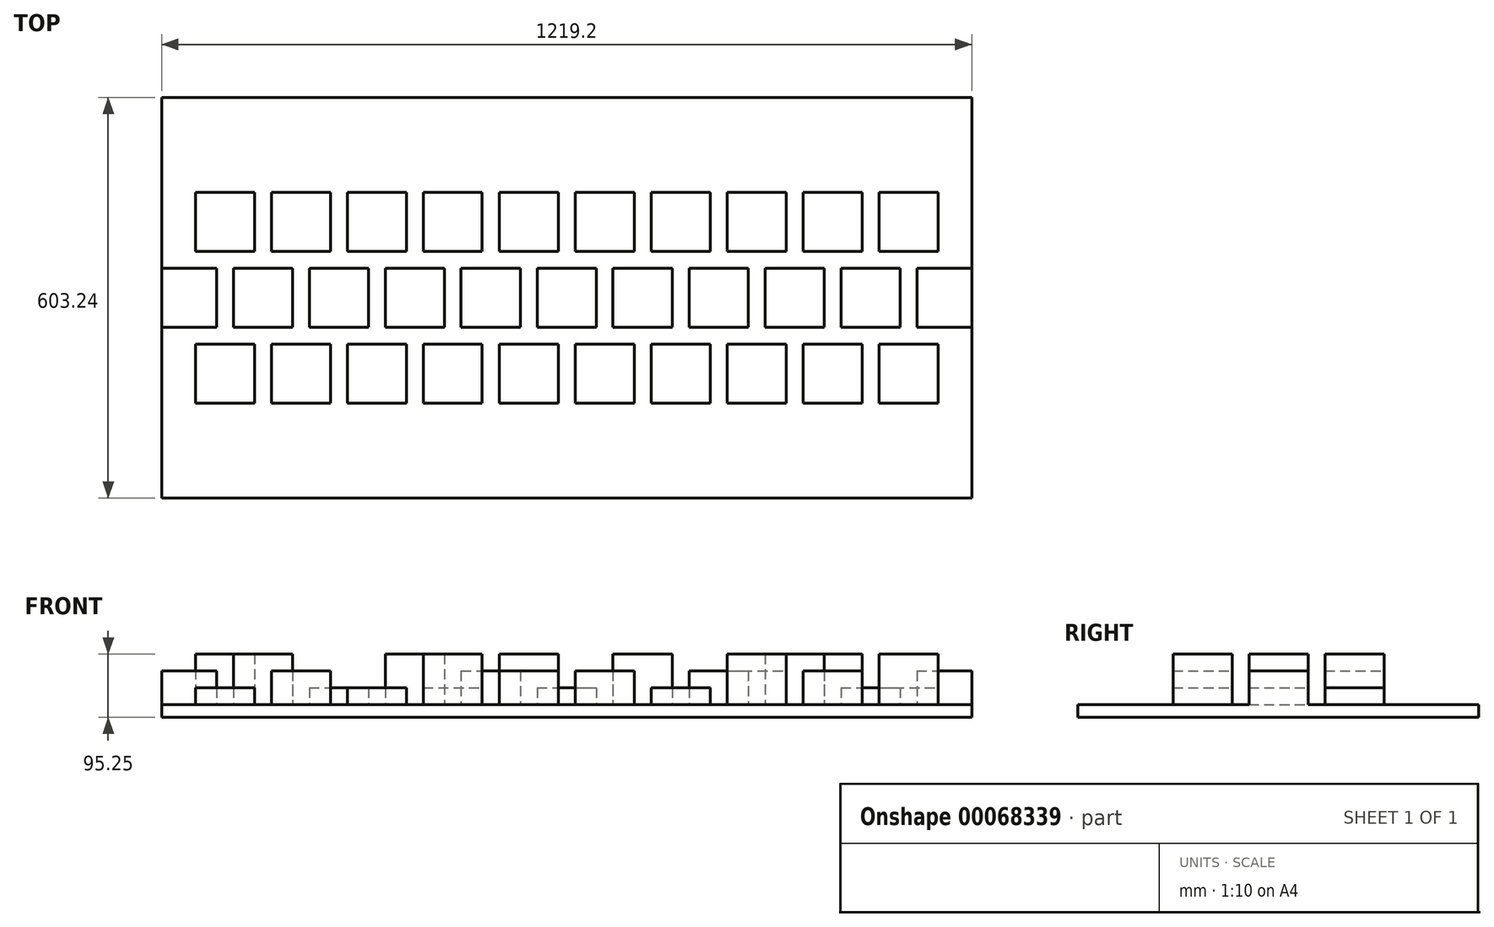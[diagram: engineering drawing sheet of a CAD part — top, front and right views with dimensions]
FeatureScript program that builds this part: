
annotation { "Feature Type Name" : "Feature", "Feature Type Description" : "" }
export const myFeature = defineFeature(function(context is Context, id is Id, definition is map)
    precondition{}
    {
        {
            var Q0;
            Q0=qCreatedBy(makeId("Top.planeOp"),FACE);
            var sketch = newSketch(context, id + "F0", { "sketchPlane" : qUnion([Q0])});
            skLineSegment(sketch, "E0.rect.bottom", {"start": v(-609.6, 301.63) * mm, "end": v(609.6, 301.63) * mm});
            skLineSegment(sketch, "E0.rect.top", {"start": v(-609.6, -301.63) * mm, "end": v(609.6, -301.63) * mm});
            skLineSegment(sketch, "E0.rect.left", {"start": v(-609.6, 301.63) * mm, "end": v(-609.6, -301.62) * mm});
            skLineSegment(sketch, "E0.rect.right", {"start": v(609.6, 301.63) * mm, "end": v(609.6, -301.62) * mm});
            skPoint(sketch, "E0.rect.middle", {"position": v(0, 0) * mm});
            skLineSegment(sketch, "E1", {"start": v(-709.91, -158.62) * mm, "end": v(803.28, -158.62) * mm, "construction": true});
            skLineSegment(sketch, "E2", {"start": v(803.28, 69.98) * mm, "end": v(-709.91, 69.98) * mm, "construction": true});
            skLineSegment(sketch, "E3", {"start": v(-709.91, -44.32) * mm, "end": v(803.28, -44.32) * mm, "construction": true});
            skLineSegment(sketch, "E4.bottom", {"start": v(-558.8, -158.62) * mm, "end": v(-469.9, -158.62) * mm});
            skLineSegment(sketch, "E4.top", {"start": v(-558.8, -69.72) * mm, "end": v(-469.9, -69.72) * mm});
            skLineSegment(sketch, "E4.left", {"start": v(-558.8, -158.62) * mm, "end": v(-558.8, -69.72) * mm});
            skLineSegment(sketch, "E4.right", {"start": v(-469.9, -158.62) * mm, "end": v(-469.9, -69.72) * mm});
            skLineSegment(sketch, "E5", {"start": v(469.9, -301.62) * mm, "end": v(469.9, 301.63) * mm, "construction": true});
            skLineSegment(sketch, "E6.0.1.0", {"start": v(-558.8, 69.98) * mm, "end": v(-469.9, 69.98) * mm});
            skLineSegment(sketch, "E6.0.1.1", {"start": v(-558.8, 158.88) * mm, "end": v(-469.9, 158.88) * mm});
            skLineSegment(sketch, "E6.0.1.2", {"start": v(-469.9, 69.98) * mm, "end": v(-469.9, 158.88) * mm});
            skLineSegment(sketch, "E6.0.1.3", {"start": v(-558.8, 69.98) * mm, "end": v(-558.8, 158.88) * mm});
            skLineSegment(sketch, "E6.1.0.0", {"start": v(-444.5, -158.62) * mm, "end": v(-355.6, -158.62) * mm});
            skLineSegment(sketch, "E6.1.0.1", {"start": v(-444.5, -69.72) * mm, "end": v(-355.6, -69.72) * mm});
            skLineSegment(sketch, "E6.1.0.2", {"start": v(-355.6, -158.62) * mm, "end": v(-355.6, -69.72) * mm});
            skLineSegment(sketch, "E6.1.0.3", {"start": v(-444.5, -158.62) * mm, "end": v(-444.5, -69.72) * mm});
            skLineSegment(sketch, "E6.1.1.0", {"start": v(-444.5, 69.98) * mm, "end": v(-355.6, 69.98) * mm});
            skLineSegment(sketch, "E6.1.1.1", {"start": v(-444.5, 158.88) * mm, "end": v(-355.6, 158.88) * mm});
            skLineSegment(sketch, "E6.1.1.2", {"start": v(-355.6, 69.98) * mm, "end": v(-355.6, 158.88) * mm});
            skLineSegment(sketch, "E6.1.1.3", {"start": v(-444.5, 69.98) * mm, "end": v(-444.5, 158.88) * mm});
            skLineSegment(sketch, "E6.2.0.0", {"start": v(-330.2, -158.62) * mm, "end": v(-241.3, -158.62) * mm});
            skLineSegment(sketch, "E6.2.0.1", {"start": v(-330.2, -69.72) * mm, "end": v(-241.3, -69.72) * mm});
            skLineSegment(sketch, "E6.2.0.2", {"start": v(-241.3, -158.62) * mm, "end": v(-241.3, -69.72) * mm});
            skLineSegment(sketch, "E6.2.0.3", {"start": v(-330.2, -158.62) * mm, "end": v(-330.2, -69.72) * mm});
            skLineSegment(sketch, "E6.2.1.0", {"start": v(-330.2, 69.98) * mm, "end": v(-241.3, 69.98) * mm});
            skLineSegment(sketch, "E6.2.1.1", {"start": v(-330.2, 158.88) * mm, "end": v(-241.3, 158.88) * mm});
            skLineSegment(sketch, "E6.2.1.2", {"start": v(-241.3, 69.98) * mm, "end": v(-241.3, 158.88) * mm});
            skLineSegment(sketch, "E6.2.1.3", {"start": v(-330.2, 69.98) * mm, "end": v(-330.2, 158.88) * mm});
            skLineSegment(sketch, "E6.3.0.0", {"start": v(-215.9, -158.62) * mm, "end": v(-127, -158.62) * mm});
            skLineSegment(sketch, "E6.3.0.1", {"start": v(-215.9, -69.72) * mm, "end": v(-127, -69.72) * mm});
            skLineSegment(sketch, "E6.3.0.2", {"start": v(-127, -158.62) * mm, "end": v(-127, -69.72) * mm});
            skLineSegment(sketch, "E6.3.0.3", {"start": v(-215.9, -158.62) * mm, "end": v(-215.9, -69.72) * mm});
            skLineSegment(sketch, "E6.3.1.0", {"start": v(-215.9, 69.98) * mm, "end": v(-127, 69.98) * mm});
            skLineSegment(sketch, "E6.3.1.1", {"start": v(-215.9, 158.88) * mm, "end": v(-127, 158.88) * mm});
            skLineSegment(sketch, "E6.3.1.2", {"start": v(-127, 69.98) * mm, "end": v(-127, 158.88) * mm});
            skLineSegment(sketch, "E6.3.1.3", {"start": v(-215.9, 69.98) * mm, "end": v(-215.9, 158.88) * mm});
            skLineSegment(sketch, "E6.4.0.0", {"start": v(-101.6, -158.62) * mm, "end": v(-12.7, -158.62) * mm});
            skLineSegment(sketch, "E6.4.0.1", {"start": v(-101.6, -69.72) * mm, "end": v(-12.7, -69.72) * mm});
            skLineSegment(sketch, "E6.4.0.2", {"start": v(-12.7, -158.62) * mm, "end": v(-12.7, -69.72) * mm});
            skLineSegment(sketch, "E6.4.0.3", {"start": v(-101.6, -158.62) * mm, "end": v(-101.6, -69.72) * mm});
            skLineSegment(sketch, "E6.4.1.0", {"start": v(-101.6, 69.98) * mm, "end": v(-12.7, 69.98) * mm});
            skLineSegment(sketch, "E6.4.1.1", {"start": v(-101.6, 158.88) * mm, "end": v(-12.7, 158.88) * mm});
            skLineSegment(sketch, "E6.4.1.2", {"start": v(-12.7, 69.98) * mm, "end": v(-12.7, 158.88) * mm});
            skLineSegment(sketch, "E6.4.1.3", {"start": v(-101.6, 69.98) * mm, "end": v(-101.6, 158.88) * mm});
            skLineSegment(sketch, "E6.5.0.0", {"start": v(12.7, -158.62) * mm, "end": v(101.6, -158.62) * mm});
            skLineSegment(sketch, "E6.5.0.1", {"start": v(12.7, -69.72) * mm, "end": v(101.6, -69.72) * mm});
            skLineSegment(sketch, "E6.5.0.2", {"start": v(101.6, -158.62) * mm, "end": v(101.6, -69.72) * mm});
            skLineSegment(sketch, "E6.5.0.3", {"start": v(12.7, -158.62) * mm, "end": v(12.7, -69.72) * mm});
            skLineSegment(sketch, "E6.5.1.0", {"start": v(12.7, 69.98) * mm, "end": v(101.6, 69.98) * mm});
            skLineSegment(sketch, "E6.5.1.1", {"start": v(12.7, 158.88) * mm, "end": v(101.6, 158.88) * mm});
            skLineSegment(sketch, "E6.5.1.2", {"start": v(101.6, 69.98) * mm, "end": v(101.6, 158.88) * mm});
            skLineSegment(sketch, "E6.5.1.3", {"start": v(12.7, 69.98) * mm, "end": v(12.7, 158.88) * mm});
            skLineSegment(sketch, "E6.6.0.0", {"start": v(127, -158.62) * mm, "end": v(215.9, -158.62) * mm});
            skLineSegment(sketch, "E6.6.0.1", {"start": v(127, -69.72) * mm, "end": v(215.9, -69.72) * mm});
            skLineSegment(sketch, "E6.6.0.2", {"start": v(215.9, -158.62) * mm, "end": v(215.9, -69.72) * mm});
            skLineSegment(sketch, "E6.6.0.3", {"start": v(127, -158.62) * mm, "end": v(127, -69.72) * mm});
            skLineSegment(sketch, "E6.6.1.0", {"start": v(127, 69.98) * mm, "end": v(215.9, 69.98) * mm});
            skLineSegment(sketch, "E6.6.1.1", {"start": v(127, 158.88) * mm, "end": v(215.9, 158.88) * mm});
            skLineSegment(sketch, "E6.6.1.2", {"start": v(215.9, 69.98) * mm, "end": v(215.9, 158.88) * mm});
            skLineSegment(sketch, "E6.6.1.3", {"start": v(127, 69.98) * mm, "end": v(127, 158.88) * mm});
            skLineSegment(sketch, "E6.7.0.0", {"start": v(241.3, -158.62) * mm, "end": v(330.2, -158.62) * mm});
            skLineSegment(sketch, "E6.7.0.1", {"start": v(241.3, -69.72) * mm, "end": v(330.2, -69.72) * mm});
            skLineSegment(sketch, "E6.7.0.2", {"start": v(330.2, -158.62) * mm, "end": v(330.2, -69.72) * mm});
            skLineSegment(sketch, "E6.7.0.3", {"start": v(241.3, -158.62) * mm, "end": v(241.3, -69.72) * mm});
            skLineSegment(sketch, "E6.7.1.0", {"start": v(241.3, 69.98) * mm, "end": v(330.2, 69.98) * mm});
            skLineSegment(sketch, "E6.7.1.1", {"start": v(241.3, 158.88) * mm, "end": v(330.2, 158.88) * mm});
            skLineSegment(sketch, "E6.7.1.2", {"start": v(330.2, 69.98) * mm, "end": v(330.2, 158.88) * mm});
            skLineSegment(sketch, "E6.7.1.3", {"start": v(241.3, 69.98) * mm, "end": v(241.3, 158.88) * mm});
            skLineSegment(sketch, "E6.8.0.0", {"start": v(355.6, -158.62) * mm, "end": v(444.5, -158.62) * mm});
            skLineSegment(sketch, "E6.8.0.1", {"start": v(355.6, -69.72) * mm, "end": v(444.5, -69.72) * mm});
            skLineSegment(sketch, "E6.8.0.2", {"start": v(444.5, -158.62) * mm, "end": v(444.5, -69.72) * mm});
            skLineSegment(sketch, "E6.8.0.3", {"start": v(355.6, -158.62) * mm, "end": v(355.6, -69.72) * mm});
            skLineSegment(sketch, "E6.8.1.0", {"start": v(355.6, 69.98) * mm, "end": v(444.5, 69.98) * mm});
            skLineSegment(sketch, "E6.8.1.1", {"start": v(355.6, 158.88) * mm, "end": v(444.5, 158.88) * mm});
            skLineSegment(sketch, "E6.8.1.2", {"start": v(444.5, 69.98) * mm, "end": v(444.5, 158.88) * mm});
            skLineSegment(sketch, "E6.8.1.3", {"start": v(355.6, 69.98) * mm, "end": v(355.6, 158.88) * mm});
            skLineSegment(sketch, "E6.9.0.0", {"start": v(469.9, -158.62) * mm, "end": v(558.8, -158.62) * mm});
            skLineSegment(sketch, "E6.9.0.1", {"start": v(469.9, -69.72) * mm, "end": v(558.8, -69.72) * mm});
            skLineSegment(sketch, "E6.9.0.2", {"start": v(558.8, -158.62) * mm, "end": v(558.8, -69.72) * mm});
            skLineSegment(sketch, "E6.9.0.3", {"start": v(469.9, -158.62) * mm, "end": v(469.9, -69.72) * mm});
            skLineSegment(sketch, "E6.9.1.0", {"start": v(469.9, 69.98) * mm, "end": v(558.8, 69.98) * mm});
            skLineSegment(sketch, "E6.9.1.1", {"start": v(469.9, 158.88) * mm, "end": v(558.8, 158.88) * mm});
            skLineSegment(sketch, "E6.9.1.2", {"start": v(558.8, 69.98) * mm, "end": v(558.8, 158.88) * mm});
            skLineSegment(sketch, "E6.9.1.3", {"start": v(469.9, 69.98) * mm, "end": v(469.9, 158.88) * mm});
            skLineSegment(sketch, "E6.direction1", {"start": v(-558.8, -158.62) * mm, "end": v(-444.5, -158.62) * mm, "construction": true});
            skLineSegment(sketch, "E6.direction2", {"start": v(-558.8, -158.62) * mm, "end": v(-558.8, 69.98) * mm, "construction": true});
            skLineSegment(sketch, "E7.bottom", {"start": v(-615.95, -44.32) * mm, "end": v(-527.05, -44.32) * mm});
            skLineSegment(sketch, "E7.top", {"start": v(-615.95, 44.58) * mm, "end": v(-527.05, 44.58) * mm});
            skLineSegment(sketch, "E7.left", {"start": v(-615.95, -44.32) * mm, "end": v(-615.95, 44.58) * mm});
            skLineSegment(sketch, "E7.right", {"start": v(-527.05, -44.32) * mm, "end": v(-527.05, 44.58) * mm});
            skLineSegment(sketch, "E8.1.0.0", {"start": v(-412.75, -44.32) * mm, "end": v(-412.75, 44.58) * mm});
            skLineSegment(sketch, "E8.1.0.1", {"start": v(-501.65, 44.58) * mm, "end": v(-412.75, 44.58) * mm});
            skLineSegment(sketch, "E8.1.0.2", {"start": v(-501.65, -44.32) * mm, "end": v(-501.65, 44.58) * mm});
            skLineSegment(sketch, "E8.1.0.3", {"start": v(-501.65, -44.32) * mm, "end": v(-412.75, -44.32) * mm});
            skLineSegment(sketch, "E8.2.0.0", {"start": v(-298.45, -44.32) * mm, "end": v(-298.45, 44.58) * mm});
            skLineSegment(sketch, "E8.2.0.1", {"start": v(-387.35, 44.58) * mm, "end": v(-298.45, 44.58) * mm});
            skLineSegment(sketch, "E8.2.0.2", {"start": v(-387.35, -44.32) * mm, "end": v(-387.35, 44.58) * mm});
            skLineSegment(sketch, "E8.2.0.3", {"start": v(-387.35, -44.32) * mm, "end": v(-298.45, -44.32) * mm});
            skLineSegment(sketch, "E8.3.0.0", {"start": v(-184.15, -44.32) * mm, "end": v(-184.15, 44.58) * mm});
            skLineSegment(sketch, "E8.3.0.1", {"start": v(-273.05, 44.58) * mm, "end": v(-184.15, 44.58) * mm});
            skLineSegment(sketch, "E8.3.0.2", {"start": v(-273.05, -44.32) * mm, "end": v(-273.05, 44.58) * mm});
            skLineSegment(sketch, "E8.3.0.3", {"start": v(-273.05, -44.32) * mm, "end": v(-184.15, -44.32) * mm});
            skLineSegment(sketch, "E8.4.0.0", {"start": v(-69.85, -44.32) * mm, "end": v(-69.85, 44.58) * mm});
            skLineSegment(sketch, "E8.4.0.1", {"start": v(-158.75, 44.58) * mm, "end": v(-69.85, 44.58) * mm});
            skLineSegment(sketch, "E8.4.0.2", {"start": v(-158.75, -44.32) * mm, "end": v(-158.75, 44.58) * mm});
            skLineSegment(sketch, "E8.4.0.3", {"start": v(-158.75, -44.32) * mm, "end": v(-69.85, -44.32) * mm});
            skLineSegment(sketch, "E8.5.0.0", {"start": v(44.45, -44.32) * mm, "end": v(44.45, 44.58) * mm});
            skLineSegment(sketch, "E8.5.0.1", {"start": v(-44.45, 44.58) * mm, "end": v(44.45, 44.58) * mm});
            skLineSegment(sketch, "E8.5.0.2", {"start": v(-44.45, -44.32) * mm, "end": v(-44.45, 44.58) * mm});
            skLineSegment(sketch, "E8.5.0.3", {"start": v(-44.45, -44.32) * mm, "end": v(44.45, -44.32) * mm});
            skLineSegment(sketch, "E8.6.0.0", {"start": v(158.75, -44.32) * mm, "end": v(158.75, 44.58) * mm});
            skLineSegment(sketch, "E8.6.0.1", {"start": v(69.85, 44.58) * mm, "end": v(158.75, 44.58) * mm});
            skLineSegment(sketch, "E8.6.0.2", {"start": v(69.85, -44.32) * mm, "end": v(69.85, 44.58) * mm});
            skLineSegment(sketch, "E8.6.0.3", {"start": v(69.85, -44.32) * mm, "end": v(158.75, -44.32) * mm});
            skLineSegment(sketch, "E8.7.0.0", {"start": v(273.05, -44.32) * mm, "end": v(273.05, 44.58) * mm});
            skLineSegment(sketch, "E8.7.0.1", {"start": v(184.15, 44.58) * mm, "end": v(273.05, 44.58) * mm});
            skLineSegment(sketch, "E8.7.0.2", {"start": v(184.15, -44.32) * mm, "end": v(184.15, 44.58) * mm});
            skLineSegment(sketch, "E8.7.0.3", {"start": v(184.15, -44.32) * mm, "end": v(273.05, -44.32) * mm});
            skLineSegment(sketch, "E8.8.0.0", {"start": v(387.35, -44.32) * mm, "end": v(387.35, 44.58) * mm});
            skLineSegment(sketch, "E8.8.0.1", {"start": v(298.45, 44.58) * mm, "end": v(387.35, 44.58) * mm});
            skLineSegment(sketch, "E8.8.0.2", {"start": v(298.45, -44.32) * mm, "end": v(298.45, 44.58) * mm});
            skLineSegment(sketch, "E8.8.0.3", {"start": v(298.45, -44.32) * mm, "end": v(387.35, -44.32) * mm});
            skLineSegment(sketch, "E8.9.0.0", {"start": v(501.65, -44.32) * mm, "end": v(501.65, 44.58) * mm});
            skLineSegment(sketch, "E8.9.0.1", {"start": v(412.75, 44.58) * mm, "end": v(501.65, 44.58) * mm});
            skLineSegment(sketch, "E8.9.0.2", {"start": v(412.75, -44.32) * mm, "end": v(412.75, 44.58) * mm});
            skLineSegment(sketch, "E8.9.0.3", {"start": v(412.75, -44.32) * mm, "end": v(501.65, -44.32) * mm});
            skLineSegment(sketch, "E8.10.0.0", {"start": v(615.95, -44.32) * mm, "end": v(615.95, 44.58) * mm});
            skLineSegment(sketch, "E8.10.0.1", {"start": v(527.05, 44.58) * mm, "end": v(615.95, 44.58) * mm});
            skLineSegment(sketch, "E8.10.0.2", {"start": v(527.05, -44.32) * mm, "end": v(527.05, 44.58) * mm});
            skLineSegment(sketch, "E8.10.0.3", {"start": v(527.05, -44.32) * mm, "end": v(615.95, -44.32) * mm});
            skLineSegment(sketch, "E8.direction1", {"start": v(-527.05, -44.32) * mm, "end": v(-412.75, -44.32) * mm, "construction": true});
            skSolve(sketch);
        }
        {
            var Q0;
            Q0=makeQuery(id+"F0.imprint","IMPRINT",FACE,{"disambiguationData":[TD([[makeQuery(id+"F0.imprint","IMPRINT",EDGE,{"derivedFrom":sQuery(id+"F0.wireOp",EDGE,"E6.1.0.0")}),1.0]])]});
            var Q1;
            Q1=makeQuery(id+"F0.imprint","IMPRINT",FACE,{"disambiguationData":[TD([[makeQuery(id+"F0.imprint","IMPRINT",EDGE,{"derivedFrom":sQuery(id+"F0.wireOp",EDGE,"E4.bottom")}),1.0]])]});
            var Q2;
            {var subQ5=sQuery(id+"F0.wireOp",EDGE,"E7.right");Q2=makeQuery(id+"F0.imprint","IMPRINT",FACE,{"disambiguationData":[TD([[makeQuery(id+"F0.imprint","IMPRINT",EDGE,{"derivedFrom":subQ5}),1.0]])]});}
            var Q3;
            Q3=makeQuery(id+"F0.imprint","IMPRINT",FACE,{"disambiguationData":[TD([[makeQuery(id+"F0.imprint","IMPRINT",EDGE,{"derivedFrom":sQuery(id+"F0.wireOp",EDGE,"E8.1.0.0")}),1.0]])]});
            var Q4;
            Q4=makeQuery(id+"F0.imprint","IMPRINT",FACE,{"disambiguationData":[TD([[makeQuery(id+"F0.imprint","IMPRINT",EDGE,{"derivedFrom":sQuery(id+"F0.wireOp",EDGE,"E6.0.1.0")}),1.0]])]});
            var Q5;
            Q5=makeQuery(id+"F0.imprint","IMPRINT",FACE,{"disambiguationData":[TD([[makeQuery(id+"F0.imprint","IMPRINT",EDGE,{"derivedFrom":sQuery(id+"F0.wireOp",EDGE,"E6.1.1.0")}),1.0]])]});
            var Q6;
            Q6=makeQuery(id+"F0.imprint","IMPRINT",FACE,{"disambiguationData":[TD([[makeQuery(id+"F0.imprint","IMPRINT",EDGE,{"derivedFrom":sQuery(id+"F0.wireOp",EDGE,"E8.2.0.0")}),1.0]])]});
            var Q7;
            Q7=makeQuery(id+"F0.imprint","IMPRINT",FACE,{"disambiguationData":[TD([[makeQuery(id+"F0.imprint","IMPRINT",EDGE,{"derivedFrom":sQuery(id+"F0.wireOp",EDGE,"E6.2.0.0")}),1.0]])]});
            var Q8;
            Q8=makeQuery(id+"F0.imprint","IMPRINT",FACE,{"disambiguationData":[TD([[makeQuery(id+"F0.imprint","IMPRINT",EDGE,{"derivedFrom":sQuery(id+"F0.wireOp",EDGE,"E6.3.0.0")}),1.0]])]});
            var Q9;
            Q9=makeQuery(id+"F0.imprint","IMPRINT",FACE,{"disambiguationData":[TD([[makeQuery(id+"F0.imprint","IMPRINT",EDGE,{"derivedFrom":sQuery(id+"F0.wireOp",EDGE,"E8.3.0.0")}),1.0]])]});
            var Q10;
            Q10=makeQuery(id+"F0.imprint","IMPRINT",FACE,{"disambiguationData":[TD([[makeQuery(id+"F0.imprint","IMPRINT",EDGE,{"derivedFrom":sQuery(id+"F0.wireOp",EDGE,"E6.2.1.0")}),1.0]])]});
            var Q11;
            Q11=makeQuery(id+"F0.imprint","IMPRINT",FACE,{"disambiguationData":[TD([[makeQuery(id+"F0.imprint","IMPRINT",EDGE,{"derivedFrom":sQuery(id+"F0.wireOp",EDGE,"E6.3.1.0")}),1.0]])]});
            var Q12;
            Q12=makeQuery(id+"F0.imprint","IMPRINT",FACE,{"disambiguationData":[TD([[makeQuery(id+"F0.imprint","IMPRINT",EDGE,{"derivedFrom":sQuery(id+"F0.wireOp",EDGE,"E8.4.0.0")}),1.0]])]});
            var Q13;
            Q13=makeQuery(id+"F0.imprint","IMPRINT",FACE,{"disambiguationData":[TD([[makeQuery(id+"F0.imprint","IMPRINT",EDGE,{"derivedFrom":sQuery(id+"F0.wireOp",EDGE,"E6.4.0.0")}),1.0]])]});
            var Q14;
            Q14=makeQuery(id+"F0.imprint","IMPRINT",FACE,{"disambiguationData":[TD([[makeQuery(id+"F0.imprint","IMPRINT",EDGE,{"derivedFrom":sQuery(id+"F0.wireOp",EDGE,"E6.5.0.0")}),1.0]])]});
            var Q15;
            Q15=makeQuery(id+"F0.imprint","IMPRINT",FACE,{"disambiguationData":[TD([[makeQuery(id+"F0.imprint","IMPRINT",EDGE,{"derivedFrom":sQuery(id+"F0.wireOp",EDGE,"E8.5.0.0")}),1.0]])]});
            var Q16;
            Q16=makeQuery(id+"F0.imprint","IMPRINT",FACE,{"disambiguationData":[TD([[makeQuery(id+"F0.imprint","IMPRINT",EDGE,{"derivedFrom":sQuery(id+"F0.wireOp",EDGE,"E6.4.1.0")}),1.0]])]});
            var Q17;
            Q17=makeQuery(id+"F0.imprint","IMPRINT",FACE,{"disambiguationData":[TD([[makeQuery(id+"F0.imprint","IMPRINT",EDGE,{"derivedFrom":sQuery(id+"F0.wireOp",EDGE,"E6.5.1.0")}),1.0]])]});
            var Q18;
            Q18=makeQuery(id+"F0.imprint","IMPRINT",FACE,{"disambiguationData":[TD([[makeQuery(id+"F0.imprint","IMPRINT",EDGE,{"derivedFrom":sQuery(id+"F0.wireOp",EDGE,"E8.6.0.0")}),1.0]])]});
            var Q19;
            Q19=makeQuery(id+"F0.imprint","IMPRINT",FACE,{"disambiguationData":[TD([[makeQuery(id+"F0.imprint","IMPRINT",EDGE,{"derivedFrom":sQuery(id+"F0.wireOp",EDGE,"E6.6.0.0")}),1.0]])]});
            var Q20;
            Q20=makeQuery(id+"F0.imprint","IMPRINT",FACE,{"disambiguationData":[TD([[makeQuery(id+"F0.imprint","IMPRINT",EDGE,{"derivedFrom":sQuery(id+"F0.wireOp",EDGE,"E6.7.0.0")}),1.0]])]});
            var Q21;
            Q21=makeQuery(id+"F0.imprint","IMPRINT",FACE,{"disambiguationData":[TD([[makeQuery(id+"F0.imprint","IMPRINT",EDGE,{"derivedFrom":sQuery(id+"F0.wireOp",EDGE,"E8.7.0.0")}),1.0]])]});
            var Q22;
            Q22=makeQuery(id+"F0.imprint","IMPRINT",FACE,{"disambiguationData":[TD([[makeQuery(id+"F0.imprint","IMPRINT",EDGE,{"derivedFrom":sQuery(id+"F0.wireOp",EDGE,"E6.6.1.0")}),1.0]])]});
            var Q23;
            Q23=makeQuery(id+"F0.imprint","IMPRINT",FACE,{"disambiguationData":[TD([[makeQuery(id+"F0.imprint","IMPRINT",EDGE,{"derivedFrom":sQuery(id+"F0.wireOp",EDGE,"E8.8.0.0")}),1.0]])]});
            var Q24;
            Q24=makeQuery(id+"F0.imprint","IMPRINT",FACE,{"disambiguationData":[TD([[makeQuery(id+"F0.imprint","IMPRINT",EDGE,{"derivedFrom":sQuery(id+"F0.wireOp",EDGE,"E6.8.0.0")}),1.0]])]});
            var Q25;
            {var subQ7=sQuery(id+"F0.wireOp",EDGE,"E0.rect.bottom");Q25=makeQuery(id+"F0.imprint","IMPRINT",FACE,{"disambiguationData":[TD([[makeQuery(id+"F0.imprint","IMPRINT",EDGE,{"derivedFrom":subQ7}),-1.0]])]});}
            var Q26;
            Q26=makeQuery(id+"F0.imprint","IMPRINT",FACE,{"disambiguationData":[TD([[makeQuery(id+"F0.imprint","IMPRINT",EDGE,{"derivedFrom":sQuery(id+"F0.wireOp",EDGE,"E6.7.1.0")}),1.0]])]});
            var Q27;
            Q27=makeQuery(id+"F0.imprint","IMPRINT",FACE,{"disambiguationData":[TD([[makeQuery(id+"F0.imprint","IMPRINT",EDGE,{"derivedFrom":sQuery(id+"F0.wireOp",EDGE,"E6.8.1.0")}),1.0]])]});
            var Q28;
            Q28=makeQuery(id+"F0.imprint","IMPRINT",FACE,{"disambiguationData":[TD([[makeQuery(id+"F0.imprint","IMPRINT",EDGE,{"derivedFrom":sQuery(id+"F0.wireOp",EDGE,"E8.9.0.0")}),1.0]])]});
            var Q29;
            Q29=makeQuery(id+"F0.imprint","IMPRINT",FACE,{"disambiguationData":[TD([[makeQuery(id+"F0.imprint","IMPRINT",EDGE,{"derivedFrom":sQuery(id+"F0.wireOp",EDGE,"E6.9.0.0")}),1.0]])]});
            var Q30;
            {var subQ5=sQuery(id+"F0.wireOp",EDGE,"E8.10.0.2");Q30=makeQuery(id+"F0.imprint","IMPRINT",FACE,{"disambiguationData":[TD([[makeQuery(id+"F0.imprint","IMPRINT",EDGE,{"derivedFrom":subQ5}),-1.0]])]});}
            var Q31;
            Q31=makeQuery(id+"F0.imprint","IMPRINT",FACE,{"disambiguationData":[TD([[makeQuery(id+"F0.imprint","IMPRINT",EDGE,{"derivedFrom":sQuery(id+"F0.wireOp",EDGE,"E6.9.1.0")}),1.0]])]});
            extrude(context, id + "F1", {"entities" : qUnion([Q0, Q1, Q2, Q3, Q4, Q5, Q6, Q7, Q8, Q9, Q10, Q11, Q12, Q13, Q14, Q15, Q16, Q17, Q18, Q19, Q20, Q21, Q22, Q23, Q24, Q25, Q26, Q27, Q28, Q29, Q30, Q31]), "oppositeDirection" : true, "depth" : 19.05 * mm});
        }
        {
            var Q0;
            Q0=makeQuery(id+"F0.imprint","IMPRINT",FACE,{"disambiguationData":[TD([[makeQuery(id+"F0.imprint","IMPRINT",EDGE,{"derivedFrom":sQuery(id+"F0.wireOp",EDGE,"E6.9.1.0")}),1.0]])]});
            var Q1;
            Q1=makeQuery(id+"F0.imprint","IMPRINT",FACE,{"disambiguationData":[TD([[makeQuery(id+"F0.imprint","IMPRINT",EDGE,{"derivedFrom":sQuery(id+"F0.wireOp",EDGE,"E8.9.0.0")}),1.0]])]});
            var Q2;
            Q2=makeQuery(id+"F0.imprint","IMPRINT",FACE,{"disambiguationData":[TD([[makeQuery(id+"F0.imprint","IMPRINT",EDGE,{"derivedFrom":sQuery(id+"F0.wireOp",EDGE,"E6.6.0.0")}),1.0]])]});
            var Q3;
            Q3=makeQuery(id+"F0.imprint","IMPRINT",FACE,{"disambiguationData":[TD([[makeQuery(id+"F0.imprint","IMPRINT",EDGE,{"derivedFrom":sQuery(id+"F0.wireOp",EDGE,"E4.bottom")}),1.0]])]});
            var Q4;
            Q4=makeQuery(id+"F0.imprint","IMPRINT",FACE,{"disambiguationData":[TD([[makeQuery(id+"F0.imprint","IMPRINT",EDGE,{"derivedFrom":sQuery(id+"F0.wireOp",EDGE,"E8.2.0.0")}),1.0]])]});
            var Q5;
            Q5=makeQuery(id+"F0.imprint","IMPRINT",FACE,{"disambiguationData":[TD([[makeQuery(id+"F0.imprint","IMPRINT",EDGE,{"derivedFrom":sQuery(id+"F0.wireOp",EDGE,"E6.2.0.0")}),1.0]])]});
            var Q6;
            Q6=makeQuery(id+"F0.imprint","IMPRINT",FACE,{"disambiguationData":[TD([[makeQuery(id+"F0.imprint","IMPRINT",EDGE,{"derivedFrom":sQuery(id+"F0.wireOp",EDGE,"E8.5.0.0")}),1.0]])]});
            var Q7;
            Q7=makeQuery(id+"F0.imprint","IMPRINT",FACE,{"disambiguationData":[TD([[makeQuery(id+"F0.imprint","IMPRINT",EDGE,{"derivedFrom":sQuery(id+"F0.wireOp",EDGE,"E6.6.1.0")}),1.0]])]});
            var Q8;
            Q8=makeQuery(id+"F0.imprint","IMPRINT",FACE,{"disambiguationData":[TD([[makeQuery(id+"F0.imprint","IMPRINT",EDGE,{"derivedFrom":sQuery(id+"F0.wireOp",EDGE,"E6.2.1.0")}),1.0]])]});
            var Q9;
            Q9=makeQuery(id+"F0.imprint","IMPRINT",FACE,{"disambiguationData":[TD([[makeQuery(id+"F0.imprint","IMPRINT",EDGE,{"derivedFrom":sQuery(id+"F0.wireOp",EDGE,"E6.3.1.0")}),1.0]])]});
            extrude(context, id + "F2", {"entities" : qUnion([Q0, Q1, Q2, Q3, Q4, Q5, Q6, Q7, Q8, Q9]), "operationType" : NewBodyOperationType.ADD, "depth" : 25.4 * mm});
        }
        {
            var Q0;
            Q0=makeQuery(id+"F0.imprint","IMPRINT",FACE,{"disambiguationData":[TD([[makeQuery(id+"F0.imprint","IMPRINT",EDGE,{"derivedFrom":sQuery(id+"F0.wireOp",EDGE,"E6.9.0.0")}),1.0]])]});
            var Q1;
            Q1=makeQuery(id+"F0.imprint","IMPRINT",FACE,{"disambiguationData":[TD([[makeQuery(id+"F0.imprint","IMPRINT",EDGE,{"derivedFrom":sQuery(id+"F0.wireOp",EDGE,"E6.8.1.0")}),1.0]])]});
            var Q2;
            Q2=makeQuery(id+"F0.imprint","IMPRINT",FACE,{"disambiguationData":[TD([[makeQuery(id+"F0.imprint","IMPRINT",EDGE,{"derivedFrom":sQuery(id+"F0.wireOp",EDGE,"E8.8.0.0")}),1.0]])]});
            var Q3;
            Q3=makeQuery(id+"F0.imprint","IMPRINT",FACE,{"disambiguationData":[TD([[makeQuery(id+"F0.imprint","IMPRINT",EDGE,{"derivedFrom":sQuery(id+"F0.wireOp",EDGE,"E8.6.0.0")}),1.0]])]});
            var Q4;
            Q4=makeQuery(id+"F0.imprint","IMPRINT",FACE,{"disambiguationData":[TD([[makeQuery(id+"F0.imprint","IMPRINT",EDGE,{"derivedFrom":sQuery(id+"F0.wireOp",EDGE,"E8.3.0.0")}),1.0]])]});
            var Q5;
            Q5=makeQuery(id+"F0.imprint","IMPRINT",FACE,{"disambiguationData":[TD([[makeQuery(id+"F0.imprint","IMPRINT",EDGE,{"derivedFrom":sQuery(id+"F0.wireOp",EDGE,"E8.1.0.0")}),1.0]])]});
            var Q6;
            Q6=makeQuery(id+"F0.imprint","IMPRINT",FACE,{"disambiguationData":[TD([[makeQuery(id+"F0.imprint","IMPRINT",EDGE,{"derivedFrom":sQuery(id+"F0.wireOp",EDGE,"E6.7.0.0")}),1.0]])]});
            var Q7;
            Q7=makeQuery(id+"F0.imprint","IMPRINT",FACE,{"disambiguationData":[TD([[makeQuery(id+"F0.imprint","IMPRINT",EDGE,{"derivedFrom":sQuery(id+"F0.wireOp",EDGE,"E6.3.0.0")}),1.0]])]});
            var Q8;
            Q8=makeQuery(id+"F0.imprint","IMPRINT",FACE,{"disambiguationData":[TD([[makeQuery(id+"F0.imprint","IMPRINT",EDGE,{"derivedFrom":sQuery(id+"F0.wireOp",EDGE,"E6.0.1.0")}),1.0]])]});
            var Q9;
            Q9=makeQuery(id+"F0.imprint","IMPRINT",FACE,{"disambiguationData":[TD([[makeQuery(id+"F0.imprint","IMPRINT",EDGE,{"derivedFrom":sQuery(id+"F0.wireOp",EDGE,"E6.4.1.0")}),1.0]])]});
            extrude(context, id + "F3", {"entities" : qUnion([Q0, Q1, Q2, Q3, Q4, Q5, Q6, Q7, Q8, Q9]), "operationType" : NewBodyOperationType.ADD, "depth" : 76.2 * mm});
        }
        {
            var Q0;
            {var subQ5=sQuery(id+"F0.wireOp",EDGE,"E7.right");Q0=makeQuery(id+"F0.imprint","IMPRINT",FACE,{"disambiguationData":[TD([[makeQuery(id+"F0.imprint","IMPRINT",EDGE,{"derivedFrom":subQ5}),1.0]])]});}
            var Q1;
            Q1=makeQuery(id+"F0.imprint","IMPRINT",FACE,{"disambiguationData":[TD([[makeQuery(id+"F0.imprint","IMPRINT",EDGE,{"derivedFrom":sQuery(id+"F0.wireOp",EDGE,"E6.1.0.0")}),1.0]])]});
            var Q2;
            Q2=makeQuery(id+"F0.imprint","IMPRINT",FACE,{"disambiguationData":[TD([[makeQuery(id+"F0.imprint","IMPRINT",EDGE,{"derivedFrom":sQuery(id+"F0.wireOp",EDGE,"E6.1.1.0")}),1.0]])]});
            var Q3;
            Q3=makeQuery(id+"F0.imprint","IMPRINT",FACE,{"disambiguationData":[TD([[makeQuery(id+"F0.imprint","IMPRINT",EDGE,{"derivedFrom":sQuery(id+"F0.wireOp",EDGE,"E6.5.1.0")}),1.0]])]});
            var Q4;
            Q4=makeQuery(id+"F0.imprint","IMPRINT",FACE,{"disambiguationData":[TD([[makeQuery(id+"F0.imprint","IMPRINT",EDGE,{"derivedFrom":sQuery(id+"F0.wireOp",EDGE,"E8.4.0.0")}),1.0]])]});
            var Q5;
            Q5=makeQuery(id+"F0.imprint","IMPRINT",FACE,{"disambiguationData":[TD([[makeQuery(id+"F0.imprint","IMPRINT",EDGE,{"derivedFrom":sQuery(id+"F0.wireOp",EDGE,"E6.4.0.0")}),1.0]])]});
            var Q6;
            Q6=makeQuery(id+"F0.imprint","IMPRINT",FACE,{"disambiguationData":[TD([[makeQuery(id+"F0.imprint","IMPRINT",EDGE,{"derivedFrom":sQuery(id+"F0.wireOp",EDGE,"E6.5.0.0")}),1.0]])]});
            var Q7;
            Q7=makeQuery(id+"F0.imprint","IMPRINT",FACE,{"disambiguationData":[TD([[makeQuery(id+"F0.imprint","IMPRINT",EDGE,{"derivedFrom":sQuery(id+"F0.wireOp",EDGE,"E8.7.0.0")}),1.0]])]});
            var Q8;
            Q8=makeQuery(id+"F0.imprint","IMPRINT",FACE,{"disambiguationData":[TD([[makeQuery(id+"F0.imprint","IMPRINT",EDGE,{"derivedFrom":sQuery(id+"F0.wireOp",EDGE,"E6.7.1.0")}),1.0]])]});
            var Q9;
            Q9=makeQuery(id+"F0.imprint","IMPRINT",FACE,{"disambiguationData":[TD([[makeQuery(id+"F0.imprint","IMPRINT",EDGE,{"derivedFrom":sQuery(id+"F0.wireOp",EDGE,"E6.8.0.0")}),1.0]])]});
            var Q10;
            {var subQ5=sQuery(id+"F0.wireOp",EDGE,"E8.10.0.2");Q10=makeQuery(id+"F0.imprint","IMPRINT",FACE,{"disambiguationData":[TD([[makeQuery(id+"F0.imprint","IMPRINT",EDGE,{"derivedFrom":subQ5}),-1.0]])]});}
            extrude(context, id + "F4", {"entities" : qUnion([Q0, Q1, Q2, Q3, Q4, Q5, Q6, Q7, Q8, Q9, Q10]), "operationType" : NewBodyOperationType.ADD, "depth" : 50.8 * mm});
        }
    });
